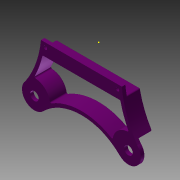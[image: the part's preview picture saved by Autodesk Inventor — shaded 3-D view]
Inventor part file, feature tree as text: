
AUTODESK INVENTOR PART (.ipt)
format: ipt  version: 2015 (Build 190159000, 159)  size: 365,568 bytes
history: native  units: mm
features: sketch x12, extrude x11, fillet x7, projected_geometry x6, plane x1
ambient origin geometry x8: Origin, YZ Plane, XZ Plane, XY Plane, X Axis, Y Axis, Z Axis, Center Point
bodies: Solid1 (feature_tree)
feature tree (37):
  extrude  "Extrusion1"  Depth=3.5mm
  extrude  "Extrusion2"  Depth=3.5mm TaperAngle=0.0deg
  extrude  "Extrusion3"  Depth=3.5mm TaperAngle=0.0deg
  extrude  "Extrusion4"  Depth=13.5mm TaperAngle=0.0deg
  extrude  "Extrusion5"  Depth=13.5mm TaperAngle=0.0deg
  extrude  "Extrusion6"  Depth=13.5mm TaperAngle=0.0deg
  extrude  "Extrusion8"  Depth=3.5mm TaperAngle=0.0deg
  extrude  "Extrusion9"  Depth=4.4125mm
  extrude  "Extrusion10"  TaperAngle=45.0deg  [1 undecoded]
  plane  "Work Plane1"
  extrude  "Extrusion11"  Depth=1.0mm
  fillet  "Fillet4"  Radius=1.0mm
  fillet  "Fillet5"  Radius=1.0mm
  fillet  "Fillet6"  Radius=1.0mm
  fillet  "Fillet7"  Radius=1.0mm
  sketch  "Sketch19"
  fillet  "Fillet8"  Radius=1.0mm
  fillet  "Fillet9"  Radius=1.0mm
  fillet  "Fillet10"  Radius=10.0mm
  extrude  "Extrusion14"  [1 undecoded]
  sketch  "Sketch1"  dims[d13=3.5mm d16=3.5mm]
  sketch  "Sketch2"  dims[d24=90.0deg d25=3.5mm d26=0.0mm]
  sketch  "Sketch3"  dims[d30=8.907301mm d32=3.5mm d33=0.0mm]
  projected_geometry  "Projected Loop1"
  sketch  "Sketch4"  dims[d34=13.5mm d35=0.0mm d38=13.5mm d39=0.0mm]
  sketch  "Sketch5"  dims[d40=31.55mm d41=13.5mm d42=0.0mm]
  projected_geometry  "Projected Loop2"
  sketch  "Sketch7"  dims[d44=3.5mm d45=0.0mm d51=13.5mm d52=0.0mm]
  projected_geometry  "Projected Loop3"
  sketch  "Sketch13"  dims[d53=3.5mm d54=0.0mm d55=3.5mm d56=0.0mm]
  projected_geometry  "Projected Loop5"
  sketch  "Sketch14"  dims[d57=0.0mm d58=4.4125mm]
  projected_geometry  "Projected Loop6"
  sketch  "Sketch15"  dims[d59=90.0deg d60=45.0deg]
  projected_geometry  "Projected Loop7"
  sketch  "Sketch16"  dims[d61=50.0mm d62=0.0mm d67=1.0mm d68=1.0mm d69=1.0mm d70=1.0mm d75=1.0mm d103=1.0mm d104=1.0mm d108=10.0mm d109=0.0mm]
  sketch  "Sketch27"
note: 2 required parameter values undecoded (feature->parameter linkage not recoverable at this tier; creation-order binding heuristic only, values carry confidence <= 0.55)
